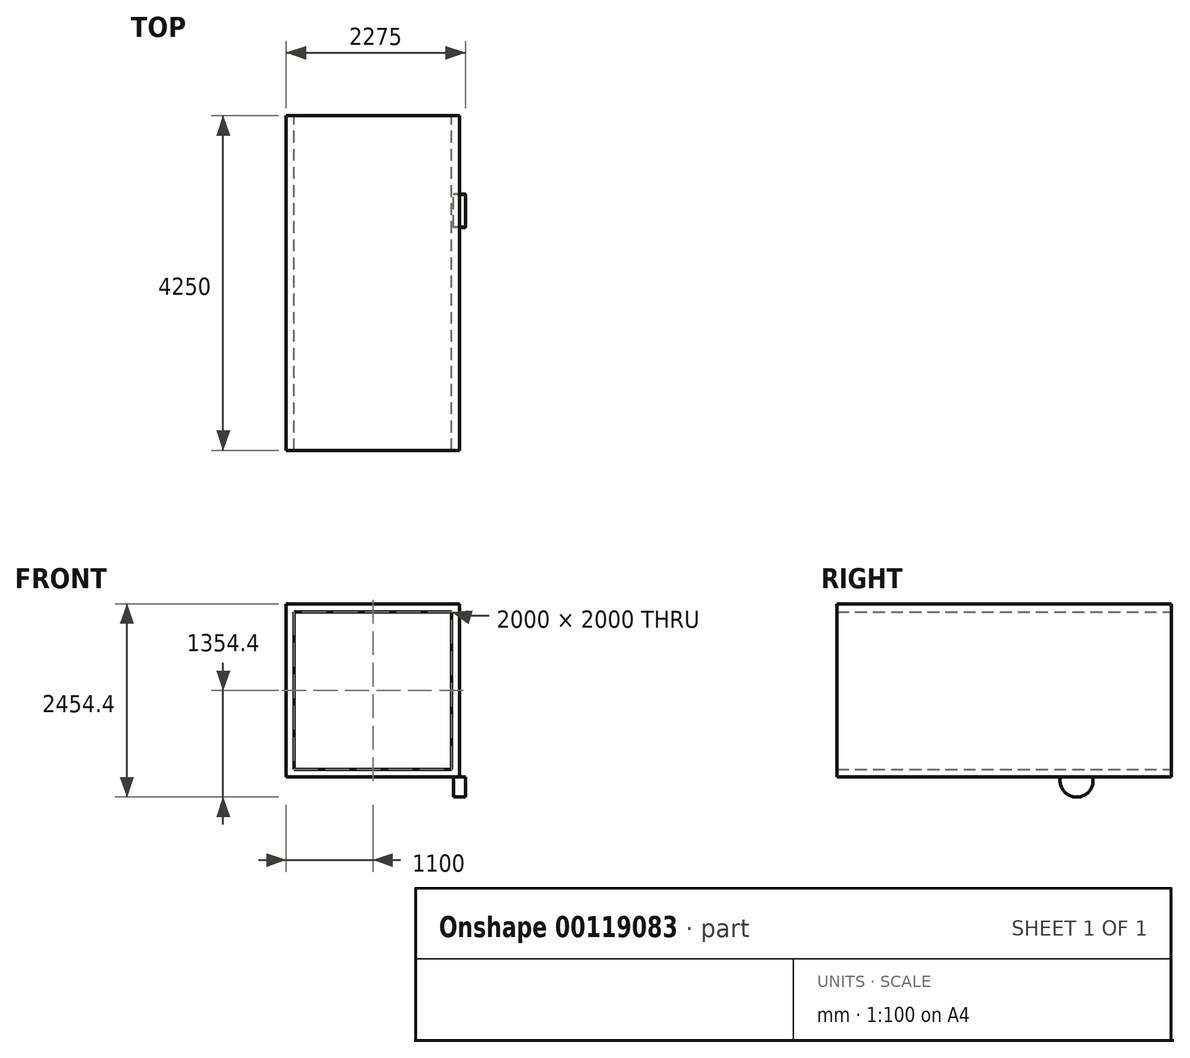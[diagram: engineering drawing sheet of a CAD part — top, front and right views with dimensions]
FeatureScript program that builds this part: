
annotation { "Feature Type Name" : "Feature", "Feature Type Description" : "" }
export const myFeature = defineFeature(function(context is Context, id is Id, definition is map)
    precondition{}
    {
        {
            var Q0;
            Q0=qCreatedBy(makeId("Front.planeOp"),FACE);
            var sketch = newSketch(context, id + "F0", { "sketchPlane" : qUnion([Q0])});
            skLineSegment(sketch, "E0.bottom", {"start": v(2100, 0) * mm, "end": v(-100, 0) * mm});
            skLineSegment(sketch, "E0.top", {"start": v(2100, 2200) * mm, "end": v(-100, 2200) * mm});
            skLineSegment(sketch, "E0.left", {"start": v(2100, 0) * mm, "end": v(2100, 2200) * mm});
            skLineSegment(sketch, "E0.right", {"start": v(-100, 0) * mm, "end": v(-100, 2200) * mm});
            skLineSegment(sketch, "E1.bottom", {"start": v(2000, 2100) * mm, "end": v(0, 2100) * mm});
            skLineSegment(sketch, "E1.top", {"start": v(2000, 100) * mm, "end": v(0, 100) * mm});
            skLineSegment(sketch, "E1.left", {"start": v(2000, 2100) * mm, "end": v(2000, 100) * mm});
            skLineSegment(sketch, "E1.right", {"start": v(0, 2100) * mm, "end": v(0, 100) * mm});
            skSolve(sketch);
        }
        {
            var Q0;
            Q0=makeQuery(id+"F0.imprint","IMPRINT",FACE,{"disambiguationData":[TD([[makeQuery(id+"F0.imprint","IMPRINT",EDGE,{"derivedFrom":sQuery(id+"F0.wireOp",EDGE,"E0.bottom")}),-1.0]])]});
            extrude(context, id + "F1", {"entities" : qUnion([Q0]), "endBound" : BoundingType.SYMMETRIC, "depth" : 4250 * mm});
        }
        {
            var Q0;
            Q0=makeQuery(id+"F1.opExtrude","SWEPT_FACE",FACE,{"disambiguationData":[OSD([sQuery(id+"F0.wireOp",EDGE,"E0.left")])]});
            var sketch = newSketch(context, id + "F2", { "sketchPlane" : qUnion([Q0])});
            skCircle(sketch, "E2", {"center": v(918.75, -44.37) * mm, "radius": 210.02 * mm});
            skSolve(sketch);
        }
        {
            var Q0;
            {var subQ0=sQuery(id+"F2.wireOp",EDGE,"E2");var subQ1=makeQuery(id+"F1.opExtrude","SWEPT_EDGE",EDGE,{"disambiguationData":[OSD([sQuery(id+"F0.wireOp",EDGE,"E0.bottom"),sQuery(id+"F0.wireOp",EDGE,"E0.left")])]});var subQ2=makeQuery(id+"F2.imprint","INTERSECT",VERTEX,{"disambiguationData":[OD(0.0)],"derivedFrom":[subQ1,subQ0]});Q0=makeQuery(id+"F2.imprint","IMPRINT",FACE,{"disambiguationData":[TD([[makeQuery(id+"F2.imprint","IMPRINT",EDGE,{"disambiguationData":[TD([[subQ2,1.0]])],"derivedFrom":subQ0}),1.0]])]});}
            extrude(context, id + "F3", {"entities" : qUnion([Q0]), "operationType" : NewBodyOperationType.ADD, "endBound" : BoundingType.SYMMETRIC, "depth" : 150 * mm});
        }
    });
